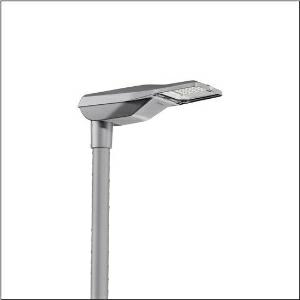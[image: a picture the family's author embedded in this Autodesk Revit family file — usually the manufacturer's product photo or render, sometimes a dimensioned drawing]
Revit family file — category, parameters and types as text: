
# Revit family: streetlight_sl_21_iq_micro___st1_0a_5xe1d41d08db_a30f
name_source: partatom
category: Lighting Fixtures
units: mm (PartAtom-declared; Revit-internal decimal feet)

## family parameters
Cut with Voids When Loaded = No
Host = Face
Light Source = No
Part Type = Normal
Room Calculation Point = No
Round Connector Dimension = Use Diameter
Shared = No

## types (1)
- --- (1 x LED, 5010 lm, 36.4 W, 4000K)
    Apparent Load = 36 VA
    CIE Flux Codes = 37 72 97 100 100
    Color Rendering = 70
    Color Temperature = 4000K
    Default Elevation = 1800 mm
    Description = Streetlight SL 21 iQ micro, mast luminaire, primary light control with lens, of PMMA, primary optical cover: cover, of toughened safety glass, transparent, light distribution: ST1.0a, light emission: direct distribution, primary light characteristic: asymmetric, installation type: post-top, side-entry, LED, High Power LED, rated luminous flux: 5.010lm, luminous efficacy: 138lm/W, light colour: 740, colour temperature: 4000K, control gear: iQ-Comfort, control: Auto-Match, Temp-Guard, Lumen-Switch, Night-Set, Smart-Wire, Light-Fading, Desk-Remote (wireless, voltage-free reading and setting of iQ features in the workshop via application-optimized NFC function/RFID function), optimised constant luminous flux control (CLO 2.0), pre-setting: linear dimming characteristic, mains connection: 220..240V, AC, 50/60Hz, start of lifetime: 36W, end of service life: 38W, reduction: 16W, luminaire housing, of diecast aluminium, powder-coated, SITECO metallic grey (DB 702S), corrosivity category C5 high according to DIN EN ISO 12944, please order mast flange separately, inclination adjustable: 0°, 5°, 10°, 15°, sealing non-destructively replaceable, multi-level sealing system, length: 528mm, width: 235mm, height: 110mm, mast flange for spigot size: 42mm (side-entry): 5XC10008XM4, 60/48mm (side-entry/post-top): 5XC10108XM2, 76/60mm (side-entry/post-top): 5XC10108XM1, protection rating (complete): IP66, insulation class (complete): insulation class II (safety insulation), certification: CE, ENEC, ENEC+, VDE, impact resistance: IK10, permissible operating ambient temperature for outdoor applications: -40..+50°C, standard-compliant lighting for roads and squares, packaging unit: 1 piece

Light Distribution: ST1.0a
    Height = 110 mm
    Lamp = 1 x LED
    Lamp Light Flux = 5010 lm
    Lamp Power = 36.4 W
    Lamp count = 1
    Length = 528 mm
    Luminous efficacy = 138 lm/W
    Manufacturer = Siteco
    ModVariant = No
    Model = 5XE1D41D08DB
    Number of Poles = 1
    OnlyDefault = Yes
    Power Factor = 1
    Product Name = Streetlight SL 21 iQ micro | ST1.0a
    Product group = mast luminaire | pylon top
    ProductGroupID = 6100
    Protection Class = Protection class II
    Protection Degree = IP 66
    RLX_Detail_Level = 1
    RLX_Emergency_Light_Flux = 0 lm
    RLX_Emergency_Type = 0
    RLX_Emergency_Type_DB = No
    RlxData = <blob elided: 98761 chars, md5=8cffbcaa>
    Socket = socket
    Standby Power = 0 W
    System Light Flux = 5010 lm
    System Power = 36 W
    Type Comments = factory setting: luminous flux: 100 % | dim-lin: 254 | 715 mA
    Type Image = l_1006881.jpg
    URL = http://relux.com
    VarID = @adj_155441
    Voltage = 0 V
    Weight = 0.00 kg
    Width = 235 mm

## geometry (parser evidence)
native form markers: Blend x4, Sweep x11
no freeform markers — native parametric forms only
